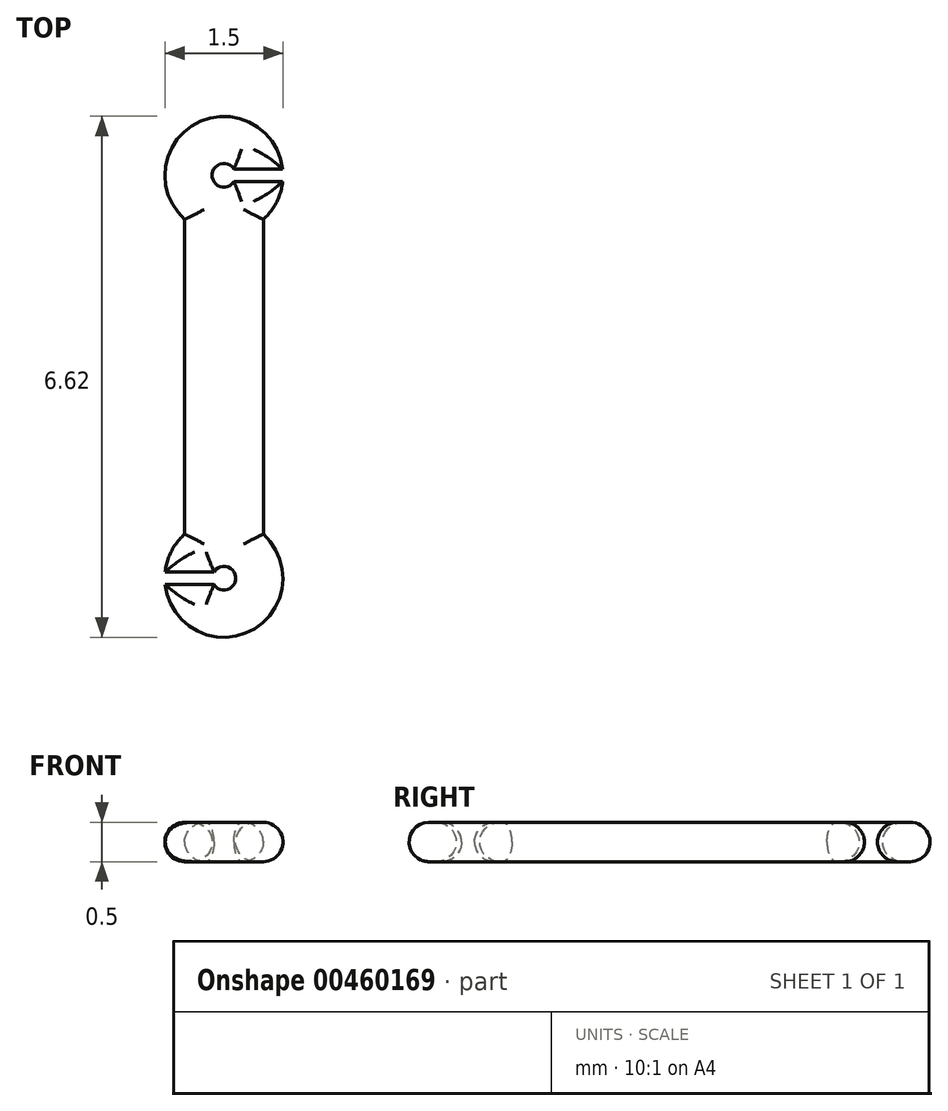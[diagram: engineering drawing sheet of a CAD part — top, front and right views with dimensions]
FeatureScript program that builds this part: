
annotation { "Feature Type Name" : "Feature", "Feature Type Description" : "" }
export const myFeature = defineFeature(function(context is Context, id is Id, definition is map)
    precondition{}
    {
        {
            var Q0;
            Q0=qCreatedBy(makeId("Top.planeOp"),FACE);
            var sketch = newSketch(context, id + "F0", { "sketchPlane" : qUnion([Q0])});
            skArc(sketch, "E0", {"start": v(0.5, 2) * mm, "mid": v(0.67, 2.22) * mm, "end": v(0.75, 2.48) * mm});
            skArc(sketch, "E1.MirrorC", {"start": v(0.5, -2) * mm, "mid": v(0.34, -3.23) * mm, "end": v(-0.75, -2.64) * mm});
            skLineSegment(sketch, "E2", {"start": v(0.5, 2) * mm, "end": v(0.5, -2) * mm});
            skLineSegment(sketch, "E3.MirrorCS", {"start": v(-0.5, 2) * mm, "end": v(-0.5, -2) * mm});
            skArc(sketch, "E4", {"start": v(0.13, 2.64) * mm, "mid": v(-0.15, 2.56) * mm, "end": v(0.13, 2.48) * mm});
            skArc(sketch, "E5.MirrorC", {"start": v(-0.13, -2.48) * mm, "mid": v(0.15, -2.56) * mm, "end": v(-0.13, -2.64) * mm});
            skLineSegment(sketch, "E6", {"start": v(0.13, 2.48) * mm, "end": v(0.75, 2.48) * mm});
            skLineSegment(sketch, "E7", {"start": v(0.13, 2.64) * mm, "end": v(0.75, 2.64) * mm});
            skLineSegment(sketch, "E8", {"start": v(-0.13, -2.48) * mm, "end": v(-0.75, -2.48) * mm});
            skLineSegment(sketch, "E9", {"start": v(-0.13, -2.64) * mm, "end": v(-0.75, -2.64) * mm});
            skArc(sketch, "E10.trimOffspring", {"start": v(-0.75, -2.48) * mm, "mid": v(-0.67, -2.22) * mm, "end": v(-0.5, -2) * mm});
            skArc(sketch, "E11.trimOffspring", {"start": v(0.75, 2.64) * mm, "mid": v(-0.34, 3.23) * mm, "end": v(-0.5, 2) * mm});
            skSolve(sketch);
        }
        {
            var Q0;
            Q0=makeQuery(id+"F0.imprint","IMPRINT",FACE,{"disambiguationData":[TD([[makeQuery(id+"F0.imprint","IMPRINT",EDGE,{"derivedFrom":sQuery(id+"F0.wireOp",EDGE,"E0")}),1.0]])]});
            extrude(context, id + "F1", {"entities" : qUnion([Q0]), "depth" : 0.5 * mm});
        }
        {
            var Q0;
            Q0=makeQuery(id+"F1.opExtrude","CAP_FACE",FACE,{"disambiguationData":[OSD([sQuery(id+"F0.wireOp",EDGE,"E0"),sQuery(id+"F0.wireOp",EDGE,"E1.MirrorC"),sQuery(id+"F0.wireOp",EDGE,"E2"),sQuery(id+"F0.wireOp",EDGE,"E3.MirrorCS"),sQuery(id+"F0.wireOp",EDGE,"E4"),sQuery(id+"F0.wireOp",EDGE,"E5.MirrorC"),sQuery(id+"F0.wireOp",EDGE,"E6"),sQuery(id+"F0.wireOp",EDGE,"E7"),sQuery(id+"F0.wireOp",EDGE,"E8"),sQuery(id+"F0.wireOp",EDGE,"E9"),sQuery(id+"F0.wireOp",EDGE,"E10.trimOffspring"),sQuery(id+"F0.wireOp",EDGE,"E11.trimOffspring")])],"isStart":true});
            var Q1;
            Q1=makeQuery(id+"F1.opExtrude","CAP_FACE",FACE,{"disambiguationData":[OSD([sQuery(id+"F0.wireOp",EDGE,"E0"),sQuery(id+"F0.wireOp",EDGE,"E1.MirrorC"),sQuery(id+"F0.wireOp",EDGE,"E2"),sQuery(id+"F0.wireOp",EDGE,"E3.MirrorCS"),sQuery(id+"F0.wireOp",EDGE,"E4"),sQuery(id+"F0.wireOp",EDGE,"E5.MirrorC"),sQuery(id+"F0.wireOp",EDGE,"E6"),sQuery(id+"F0.wireOp",EDGE,"E7"),sQuery(id+"F0.wireOp",EDGE,"E8"),sQuery(id+"F0.wireOp",EDGE,"E9"),sQuery(id+"F0.wireOp",EDGE,"E10.trimOffspring"),sQuery(id+"F0.wireOp",EDGE,"E11.trimOffspring")])],"isStart":false});
            fillet(context, id + "F2", {"entities" : qUnion([Q0, Q1]), "radius" : 0.25 * mm, "tangentPropagation" : true, "allowEdgeOverflow" : false});
        }
    });
